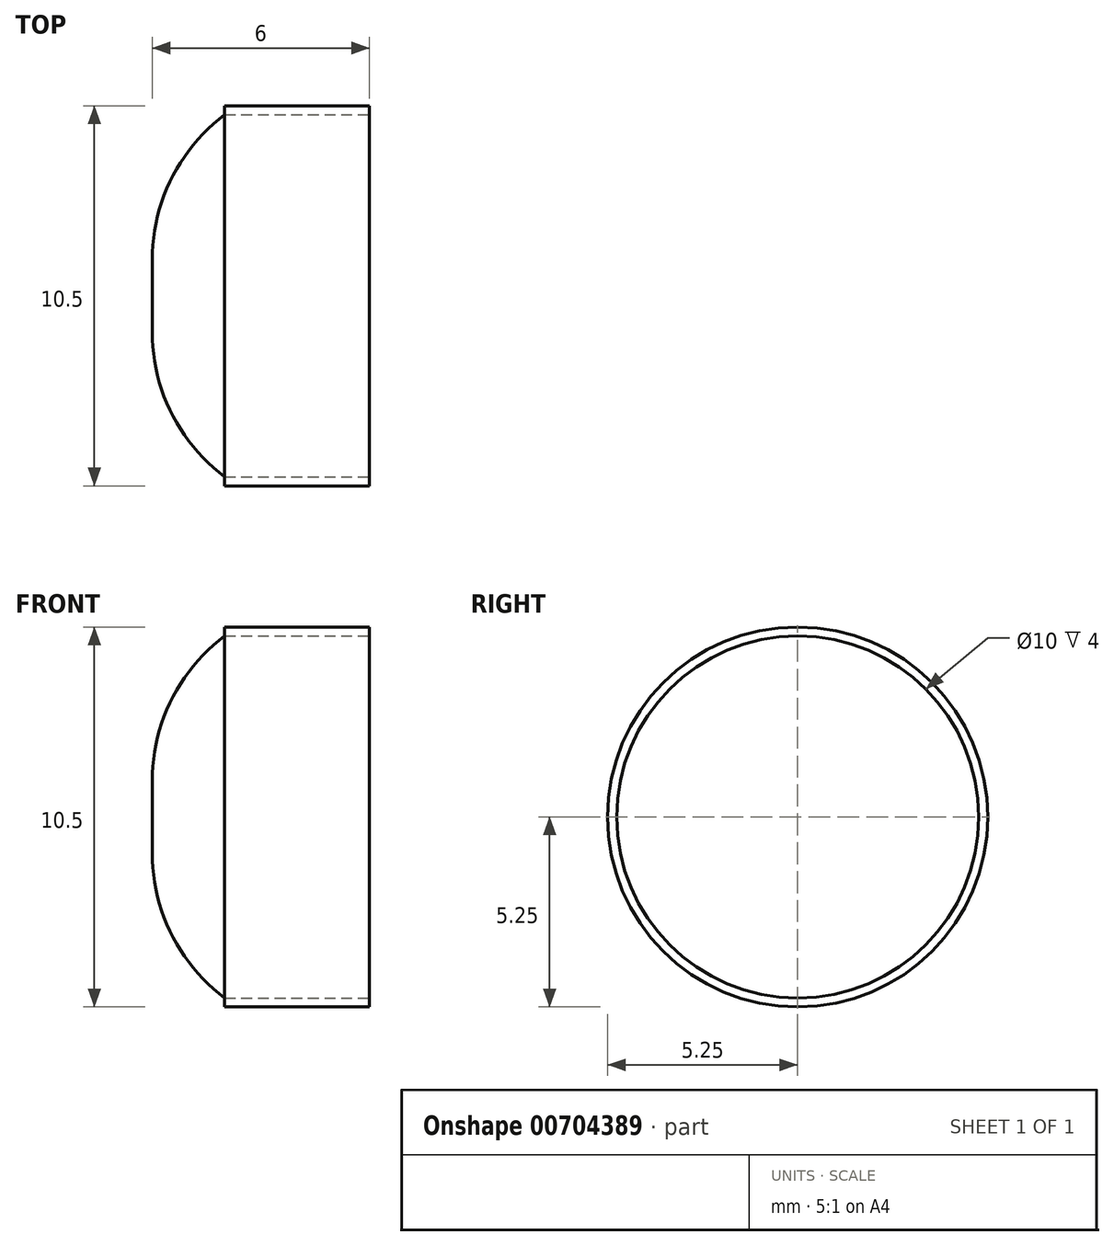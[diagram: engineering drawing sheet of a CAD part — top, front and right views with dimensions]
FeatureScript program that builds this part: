
annotation { "Feature Type Name" : "Feature", "Feature Type Description" : "" }
export const myFeature = defineFeature(function(context is Context, id is Id, definition is map)
    precondition{}
    {
        {
            var Q0;
            Q0=qCreatedBy(makeId("Front.planeOp"),FACE);
            var sketch = newSketch(context, id + "F0", { "sketchPlane" : qUnion([Q0])});
            skLineSegment(sketch, "E0", {"start": v(0, 0) * mm, "end": v(-6, 0) * mm});
            skLineSegment(sketch, "E1.bottom", {"start": v(0, 0) * mm, "end": v(-4, 0) * mm});
            skLineSegment(sketch, "E1.top", {"start": v(0, 5.25) * mm, "end": v(-4, 5.25) * mm});
            skLineSegment(sketch, "E1.left", {"start": v(0, 0) * mm, "end": v(0, 5.25) * mm});
            skLineSegment(sketch, "E1.right", {"start": v(-4, 0) * mm, "end": v(-4, 5.25) * mm});
            skLineSegment(sketch, "E2.top", {"start": v(0, 5) * mm, "end": v(-6, 5) * mm});
            skLineSegment(sketch, "E2.left", {"start": v(0, 0) * mm, "end": v(0, 5) * mm});
            skLineSegment(sketch, "E2.right", {"start": v(-6, 0) * mm, "end": v(-6, 5) * mm});
            skLineSegment(sketch, "E3.MirrorCS", {"start": v(-6, 0) * mm, "end": v(-6, -5) * mm});
            skLineSegment(sketch, "E4.MirrorCS", {"start": v(0, -5.25) * mm, "end": v(-4, -5.25) * mm});
            skLineSegment(sketch, "E5.MirrorCS", {"start": v(0, 0) * mm, "end": v(0, -5) * mm});
            skLineSegment(sketch, "E6.MirrorCS", {"start": v(0, -5) * mm, "end": v(-6, -5) * mm});
            skLineSegment(sketch, "E7.MirrorCS", {"start": v(0, 0) * mm, "end": v(0, -5.25) * mm});
            skLineSegment(sketch, "E8.MirrorCS", {"start": v(-4, 0) * mm, "end": v(-4, -5.25) * mm});
            skPoint(sketch, "E9", {"position": v(0, 0) * mm});
            skSolve(sketch);
        }
        {
            var Q0;
            {var subQ5=sQuery(id+"F0.wireOp",EDGE,"E2.left");Q0=makeQuery(id+"F0.imprint","IMPRINT",FACE,{"disambiguationData":[TD([[makeQuery(id+"F0.imprint","IMPRINT",EDGE,{"derivedFrom":subQ5}),1.0]])]});}
            var Q1;
            {var subQ5=sQuery(id+"F0.wireOp",EDGE,"E2.right");Q1=makeQuery(id+"F0.imprint","IMPRINT",FACE,{"disambiguationData":[TD([[makeQuery(id+"F0.imprint","IMPRINT",EDGE,{"derivedFrom":subQ5}),-1.0]])]});}
            var Q2;
            {var subQ0=sQuery(id+"F0.wireOp",EDGE,"E1.top");Q2=makeQuery(id+"F0.imprint","IMPRINT",FACE,{"disambiguationData":[TD([[makeQuery(id+"F0.imprint","IMPRINT",EDGE,{"derivedFrom":subQ0}),1.0]])]});}
            var Q3;
            Q3=sQuery(id+"F0.wireOp",EDGE,"E0");
            revolve(context, id + "F1", {"surfaceOperationType" : NewSurfaceOperationType.NEW, "entities" : qUnion([Q0, Q1, Q2]), "axis" : qUnion([Q3]), "revolveType" : RevolveType.FULL});
        }
        {
            var Q0;
            Q0=makeQuery(id+"F1.opRevolve","SWEPT_EDGE",EDGE,{"disambiguationData":[OSD([sQuery(id+"F0.wireOp",EDGE,"E2.top"),sQuery(id+"F0.wireOp",EDGE,"E2.right")])]});
            fillet(context, id + "F2", {"entities" : qUnion([Q0]), "radius" : 5 * mm, "tangentPropagation" : true, "allowEdgeOverflow" : false});
        }
    });
